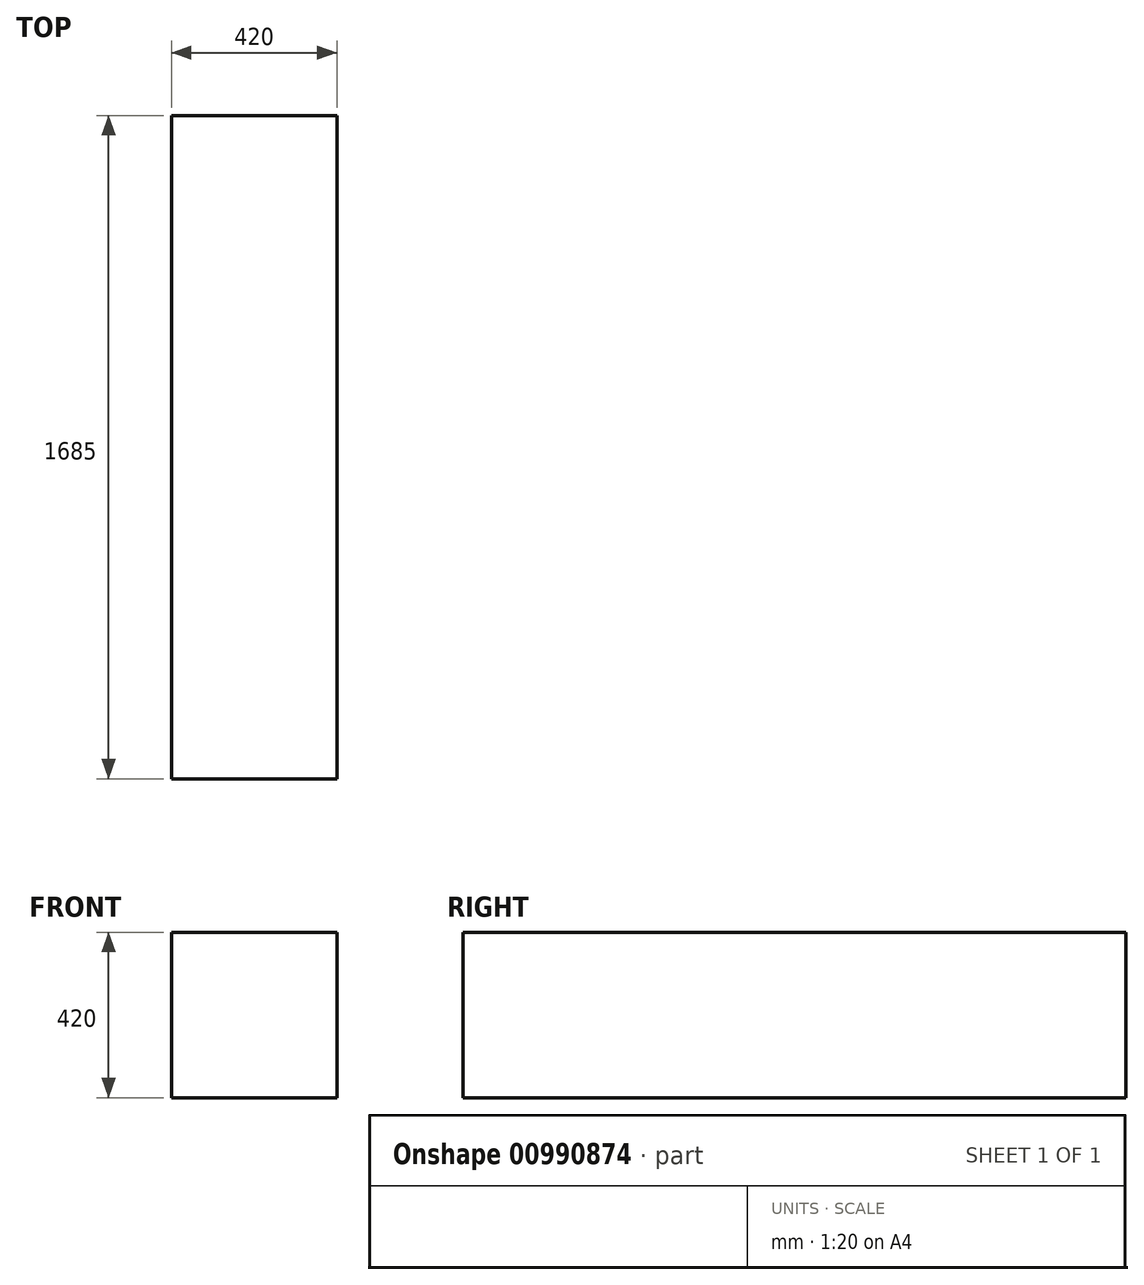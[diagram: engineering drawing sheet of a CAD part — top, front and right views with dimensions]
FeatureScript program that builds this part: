
annotation { "Feature Type Name" : "Feature", "Feature Type Description" : "" }
export const myFeature = defineFeature(function(context is Context, id is Id, definition is map)
    precondition{}
    {
        {
            var Q0;
            Q0=qCreatedBy(makeId("Top.planeOp"),FACE);
            var sketch = newSketch(context, id + "F0", { "sketchPlane" : qUnion([Q0])});
            skLineSegment(sketch, "E0.bottom", {"start": v(0, 0) * mm, "end": v(420, 0) * mm});
            skLineSegment(sketch, "E0.top", {"start": v(0, 1685) * mm, "end": v(420, 1685) * mm});
            skLineSegment(sketch, "E0.left", {"start": v(0, 0) * mm, "end": v(0, 1685) * mm});
            skLineSegment(sketch, "E0.right", {"start": v(420, 0) * mm, "end": v(420, 1685) * mm});
            skSolve(sketch);
        }
        {
            var Q0;
            Q0=makeQuery(id+"F0.imprint","IMPRINT",FACE,{"disambiguationData":[TD([[makeQuery(id+"F0.imprint","IMPRINT",EDGE,{"derivedFrom":sQuery(id+"F0.wireOp",EDGE,"E0.bottom")}),1.0]])]});
            extrude(context, id + "F1", {"entities" : qUnion([Q0]), "depth" : 420 * mm, "offsetDistance" : 25 * mm});
        }
    });
